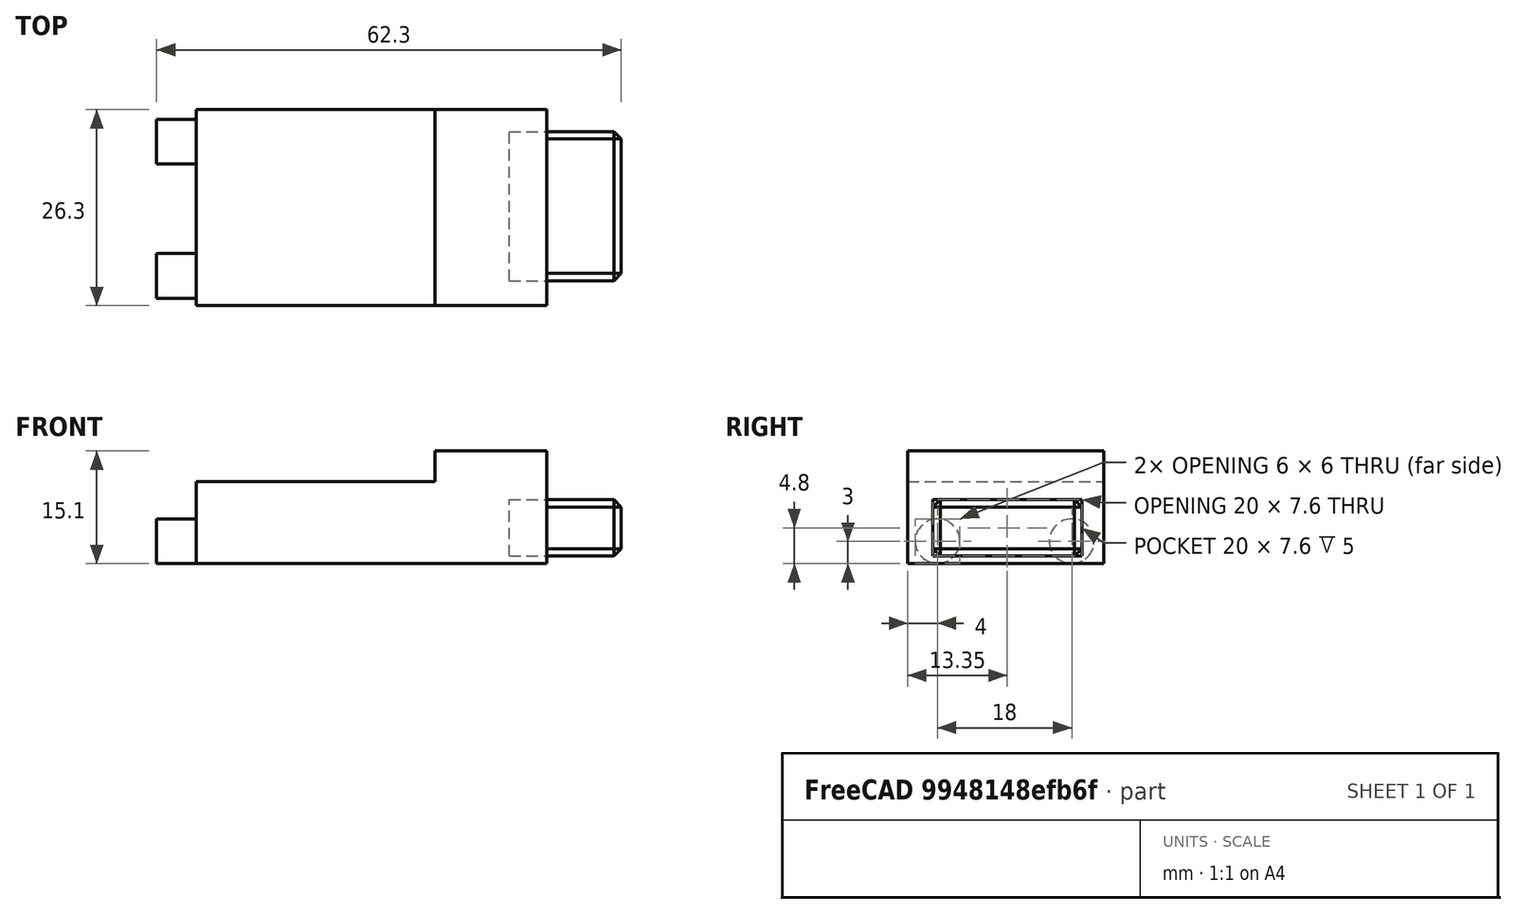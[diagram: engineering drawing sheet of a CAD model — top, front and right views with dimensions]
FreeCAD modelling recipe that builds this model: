
FCSTD DOCUMENT  (FreeCAD 0.18R4 (GitTag))
Label: Receiver
License: All rights reserved
LicenseURL: http://en.wikipedia.org/wiki/All_rights_reserved
objects: Part::Box×4, Part::Feature×3, Part::Cylinder×2, Part::MultiFuse×2, Part::Cut×1, Part::Chamfer×1
note: 13 computed .brp shape members not serialized (recipe doc carries the construction recipe); baked Part::Feature solids carry a one-line shape summary decoded from their .brp

FEATURE [Part::Box] Box  label="Cube"
  AttacherType = Attacher::AttachEngine3D
  Height = 11
  Length = 47
  Width = 26.3
FEATURE [Part::Box] Box001  label="Cube001"
  AttacherType = Attacher::AttachEngine3D
  Height = 15.1
  Length = 15
  Placement = pos=(32,0,0) rot=(0,0,1;0rad)
  Width = 26.3
FEATURE [Part::Cylinder] Cylinder
  Angle = 360
  AttacherType = Attacher::AttachEngine3D
  Height = 5.3
  Placement = pos=(0,4,3) rot=(0,1,0;-1.5708rad)
  Radius = 3
FEATURE [Part::Cylinder] Cylinder001
  Angle = 360
  AttacherType = Attacher::AttachEngine3D
  Height = 5.3
  Placement = pos=(0,22,3) rot=(0,-1,0;1.5708rad)
  Radius = 3
FEATURE [Part::Box] Box002  label="Plugs"
  AttacherType = Attacher::AttachEngine3D
  Height = 7.6
  Length = 5
  Placement = pos=(42,3.35,1) rot=(0,0,1;0rad)
  Width = 20
FEATURE [Part::MultiFuse] Fusion  label="Body01"
  Shapes = -> [Box,Box001,Cylinder,Cylinder001]
FEATURE [Part::Cut] Cut  label="Receiver (Model)"
  Base = -> Fusion
  Tool = -> Box002
FEATURE [Part::Box] Box003  label="Plugs001"
  AttacherType = Attacher::AttachEngine3D
  Height = 7.6
  Length = 15
  Placement = pos=(42,3.35,1) rot=(0,0,1;0rad)
  Width = 20
FEATURE [Part::Feature] Cut_solid  label="Receiver (Solid)"
  shape: bbox 52.3 x 26.3 x 15.1 mm, 23 faces (baked)
FEATURE [Part::Feature] Cut_solid001  label="Receiver With Plug Allowance"
  shape: bbox 52.3 x 26.3 x 15.1 mm, 23 faces (baked)
FEATURE [Part::MultiFuse] Fusion001  label="Reciver With Plug Allowance (Model)"
  Shapes = -> [Cut_solid001,Box003]
FEATURE [Part::Chamfer] Chamfer  label="Receiver With Plug Allowance (Model)"
  Base = -> Fusion001
  Edges = 8 edges r=1: [Edge43,Edge44,Edge45,Edge46,Edge47,Edge48,Edge49,Edge50]
FEATURE [Part::Feature] Chamfer_solid  label="Receiver With Plug Allowance (Solid)"
  shape: bbox 62.3 x 26.3 x 15.1 mm, 35 faces (baked)
